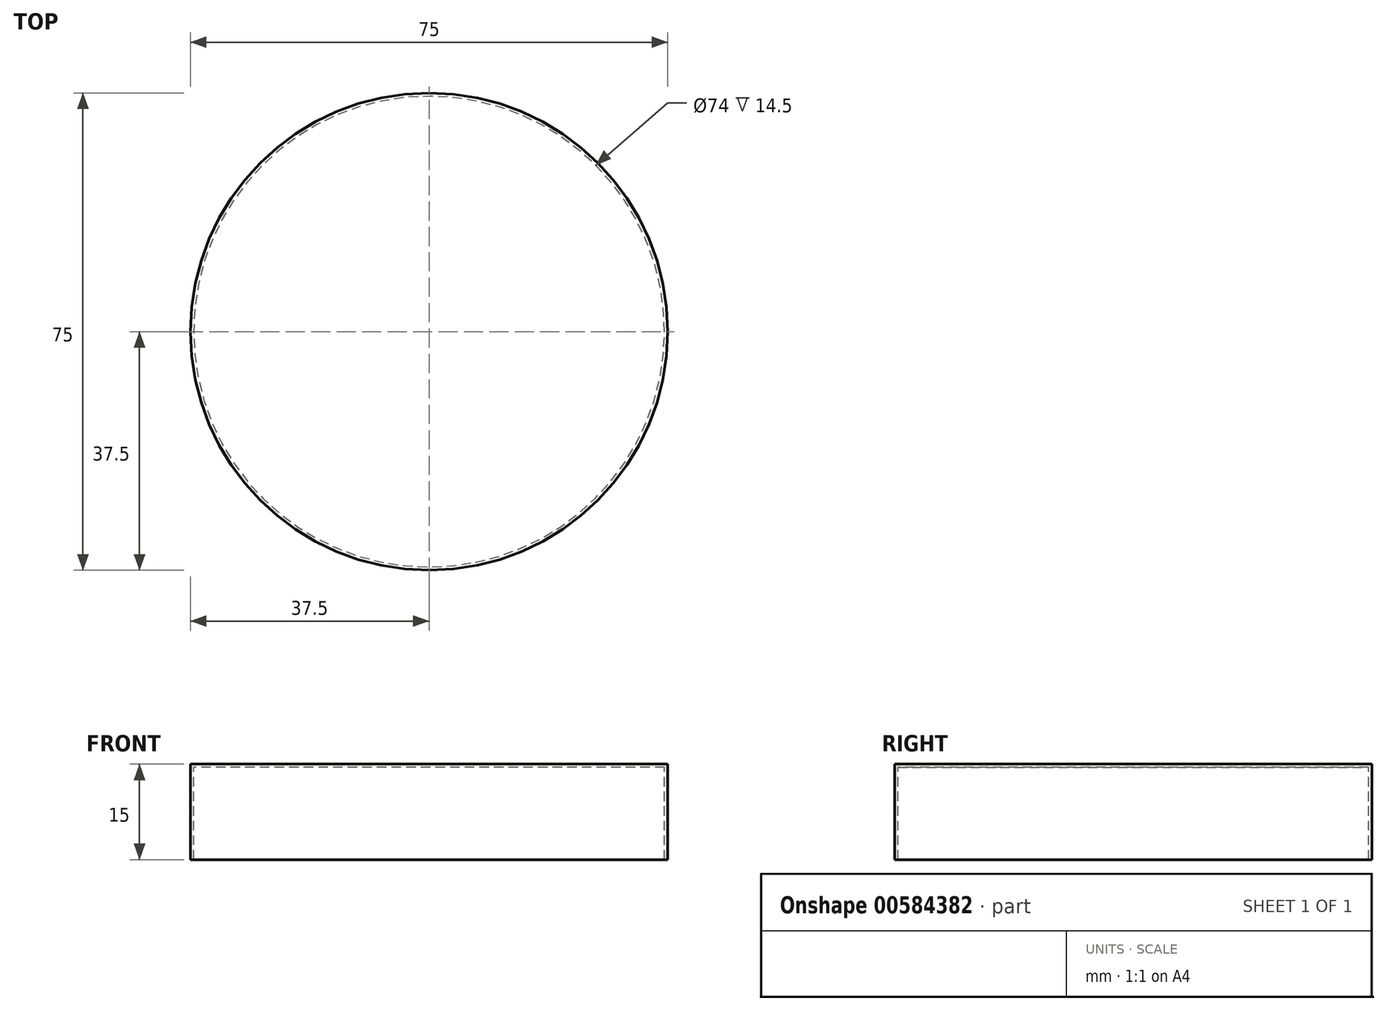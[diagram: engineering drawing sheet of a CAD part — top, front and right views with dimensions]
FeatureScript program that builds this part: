
annotation { "Feature Type Name" : "Feature", "Feature Type Description" : "" }
export const myFeature = defineFeature(function(context is Context, id is Id, definition is map)
    precondition{}
    {
        {
            var Q0;
            Q0=qCreatedBy(makeId("Front.planeOp"),FACE);
            var sketch = newSketch(context, id + "F0", { "sketchPlane" : qUnion([Q0])});
            skLineSegment(sketch, "E0.bottom", {"start": v(37.5, -7.5) * mm, "end": v(-37.5, -7.5) * mm});
            skLineSegment(sketch, "E0.top", {"start": v(37.5, 7.5) * mm, "end": v(-37.5, 7.5) * mm});
            skLineSegment(sketch, "E0.left", {"start": v(37.5, -7.5) * mm, "end": v(37.5, 7.5) * mm});
            skLineSegment(sketch, "E0.right", {"start": v(-37.5, -7.5) * mm, "end": v(-37.5, 7.5) * mm});
            skPoint(sketch, "E0.middle", {"position": v(0, 0) * mm});
            skLineSegment(sketch, "E1.top", {"start": v(-38.82, 0) * mm, "end": v(37.98, 0) * mm});
            skLineSegment(sketch, "E2", {"start": v(0, 32.32) * mm, "end": v(0, -32.54) * mm});
            skSolve(sketch);
        }
        {
            var Q0;
            {var subQ0=sQuery(id+"F0.wireOp",EDGE,"50Q9B2Dz-tjYX-buu7-mBbi-ssvcsfGVtirO");Q0=makeQuery(id+"F0.imprint","IMPRINT",FACE,{"disambiguationData":[TD([[makeQuery(id+"F0.imprint","IMPRINT",EDGE,{"derivedFrom":subQ0}),1.0]])]});}
            var Q1;
            {var subQ0=sQuery(id+"F0.wireOp",EDGE,"E0.right");var subQ1=sQuery(id+"F0.wireOp",EDGE,"E0.bottom");var subQ2=makeQuery(id+"F0.imprint","INTERSECT",VERTEX,{"derivedFrom":[subQ1,subQ0]});Q1=makeQuery(id+"F0.imprint","IMPRINT",FACE,{"disambiguationData":[TD([[makeQuery(id+"F0.imprint","IMPRINT",EDGE,{"disambiguationData":[TD([[subQ2,1.0]])],"derivedFrom":subQ1}),-1.0]])]});}
            var Q2;
            {var subQ0=sQuery(id+"F0.wireOp",EDGE,"E0.right");var subQ1=sQuery(id+"F0.wireOp",EDGE,"E0.top");var subQ2=makeQuery(id+"F0.imprint","INTERSECT",VERTEX,{"derivedFrom":[subQ1,subQ0]});Q2=makeQuery(id+"F0.imprint","IMPRINT",FACE,{"disambiguationData":[TD([[makeQuery(id+"F0.imprint","IMPRINT",EDGE,{"disambiguationData":[TD([[subQ2,1.0]])],"derivedFrom":subQ1}),1.0]])]});}
            var Q3;
            Q3=sQuery(id+"F0.wireOp",EDGE,"E2");
            revolve(context, id + "F1", {"entities" : qUnion([Q0, Q1, Q2]), "axis" : qUnion([Q3]), "revolveType" : RevolveType.FULL});
        }
        {
            var Q0;
            Q0=makeQuery(id+"F1.opRevolve","SWEPT_FACE",FACE,{"disambiguationData":[OSD([sQuery(id+"F0.wireOp",EDGE,"E0.bottom")])]});
            shell(context, id + "F2", {"entities" : qUnion([Q0]), "thickness" : 0.5 * mm});
        }
    });
